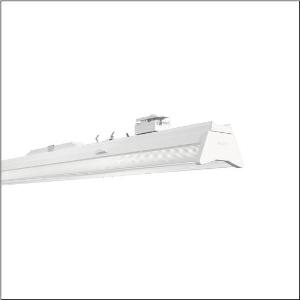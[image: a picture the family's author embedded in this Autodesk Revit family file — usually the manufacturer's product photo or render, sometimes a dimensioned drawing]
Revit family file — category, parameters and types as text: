
# Revit family: licross_r__21_performance_mo_52td167n445g_3390
name_source: partatom
category: Lighting Fixtures
units: mm (PartAtom-declared; Revit-internal decimal feet)

## family parameters
Cut with Voids When Loaded = No
Host = Face
Light Source = No
Part Type = Normal
Room Calculation Point = No
Round Connector Dimension = Use Diameter
Shared = No

## types (1)
- Licross® 21 Performance MO (1 x LED, 4580 lm, 24.7 W, 4000K)
    Apparent Load = 25 VA
    CIE Flux Codes = 66 88 96 79 100
    Color Rendering = 80
    Color Temperature = 4000K
    Default Elevation = 1800 mm
    Description = Licross® 21 Performance MO, luminaire insert, of sheet steel, galvanised, coil coated, white, length: 1.500mm, width: 120mm, height: 123mm, LED rated luminous flux: 4.580lm, light colour: 840, control gear: ON/OFF, with plug, 3-pole, with phase selection, mains connection: 220..240V, AC, 50/60Hz, rated input power: 25W, halogen-free wiring, primary light control with lens, of plastic, primary optical cover: cover, of PMMA, CAT 2 (L<= 3000cd/m²), light emission: direct/indirect distribution, primary light characteristic: symmetric, protection rating (complete): IP54, insulation class (complete): insulation class I (protective earthing), certification: CE, ENEC, UKCA, protection symbol: D if used in an environment with non-conductive dust loads with corresponding accessories, impact resistance: IK06, permissible ambient temperature for indoor applications: -35..+55°C, corresponds to IFS (International Featured Standards) requirements for safety and quality in the food industry, reducing of maximum allowable ambient temperature of 5°C with ceiling mounting, LABS conformity tested according to VDMA 24364:2018-05, packaging unit: 1 piece
    Height = 114 mm
    Lamp = 1 x LED
    Lamp Light Flux = 4580 lm
    Lamp Power = 24.7 W
    Lamp count = 1
    Length = 1500 mm
    Luminous efficacy = 185 lm/W
    Manufacturer = Siteco
    ModVariant = No
    Model = 52TD167N445G
    Mounting Place = Ceiling
    Mounting Type = Pendant
    Number of Poles = 1
    OnlyDefault = Yes
    Power Factor = 1
    Product Name = Licross® 21 Performance MO
    Product group = luminaire insert
    ProductGroupID = 901
    Protection Class = Protection class I
    Protection Degree = IP 54
    RLX_Detail_Level = 1
    RLX_Emergency_Light_Flux = 0 lm
    RLX_Emergency_Type = 0
    RLX_Emergency_Type_DB = No
    RlxData = <blob elided: 30449 chars, md5=63216319>
    Socket = socket
    Standby Power = 0 W
    System Light Flux = 4580 lm
    System Power = 25 W
    Type Comments = Product without accessories
    Type Image = l_1256138.jpg
    URL = http://relux.com
    VarID = ---
    Voltage = 0 V
    Weight = 0.00 kg
    Width = 120 mm

## geometry (parser evidence)
native form markers: Blend x4, Sweep x12
no freeform markers — native parametric forms only
